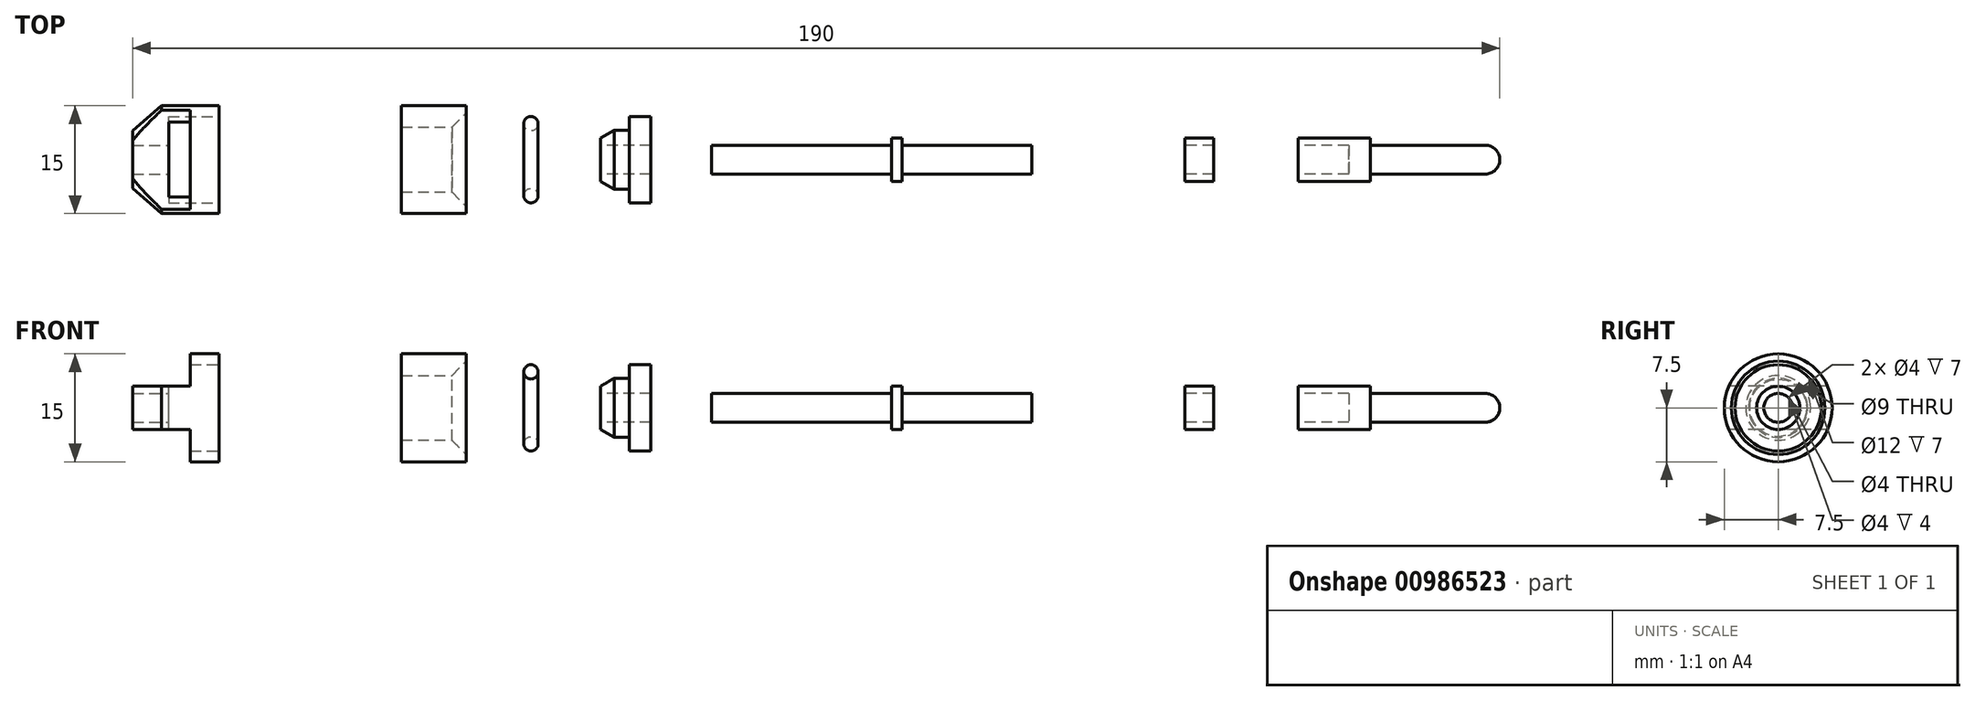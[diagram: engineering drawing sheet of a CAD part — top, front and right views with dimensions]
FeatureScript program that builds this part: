
annotation { "Feature Type Name" : "Feature", "Feature Type Description" : "" }
export const myFeature = defineFeature(function(context is Context, id is Id, definition is map)
    precondition{}
    {
        {
            var Q0;
            Q0=qCreatedBy(makeId("Front.planeOp"),FACE);
            var sketch = newSketch(context, id + "F0", { "sketchPlane" : qUnion([Q0])});
            skLineSegment(sketch, "E0", {"start": v(0, 2) * mm, "end": v(0, 6) * mm});
            skLineSegment(sketch, "E1", {"start": v(0, 6) * mm, "end": v(-3, 6) * mm});
            skLineSegment(sketch, "E2", {"start": v(-7, 3) * mm, "end": v(-7, 2) * mm});
            skLineSegment(sketch, "E3", {"start": v(-7, 2) * mm, "end": v(0, 2) * mm});
            skLineSegment(sketch, "E4", {"start": v(-20.87, 0) * mm, "end": v(7.44, 0) * mm, "construction": true});
            skLineSegment(sketch, "E5", {"start": v(-5.1, 4.1) * mm, "end": v(-3, 4.1) * mm});
            skLineSegment(sketch, "E6", {"start": v(-3, 6) * mm, "end": v(-3, 4.1) * mm});
            skLineSegment(sketch, "E7.trimOffspring", {"start": v(-5.1, 4.1) * mm, "end": v(-7, 3) * mm});
            skCircle(sketch, "E8", {"center": v(-4, 5.1) * mm, "radius": 1 * mm, "construction": true});
            skSolve(sketch);
        }
        {
            var Q0;
            Q0 = qSketchRegion(id + "F0", true);
            var Q1;
            Q1=sQuery(id+"F0.wireOp",EDGE,"E4");
            revolve(context, id + "F1", {"surfaceOperationType" : NewSurfaceOperationType.NEW, "entities" : qUnion([Q0]), "axis" : qUnion([Q1]), "revolveType" : RevolveType.FULL});
        }
        {
            var Q0;
            Q0=qCreatedBy(makeId("Front.planeOp"),FACE);
            var sketch = newSketch(context, id + "F2", { "sketchPlane" : qUnion([Q0])});
            skCircle(sketch, "E9", {"center": v(-16.65, 5) * mm, "radius": 1 * mm});
            skLineSegment(sketch, "E10", {"start": v(-20.47, 0) * mm, "end": v(-13.32, 0) * mm, "construction": true});
            skSolve(sketch);
        }
        {
            var Q0;
            Q0 = qSketchRegion(id + "F2", true);
            var Q1;
            Q1=sQuery(id+"F2.wireOp",EDGE,"E10");
            revolve(context, id + "F3", {"surfaceOperationType" : NewSurfaceOperationType.NEW, "entities" : qUnion([Q0]), "axis" : qUnion([Q1]), "revolveType" : RevolveType.FULL});
        }
        {
            var Q0;
            Q0=qCreatedBy(makeId("Front.planeOp"),FACE);
            var sketch = newSketch(context, id + "F4", { "sketchPlane" : qUnion([Q0])});
            skLineSegment(sketch, "E11", {"start": v(-21.56, 0) * mm, "end": v(-45.94, 0) * mm, "construction": true});
            skLineSegment(sketch, "E12", {"start": v(-27.65, 4.5) * mm, "end": v(-34.65, 4.5) * mm});
            skLineSegment(sketch, "E13", {"start": v(-34.65, 4.5) * mm, "end": v(-34.65, 7.5) * mm});
            skLineSegment(sketch, "E14", {"start": v(-34.65, 7.5) * mm, "end": v(-25.65, 7.5) * mm});
            skLineSegment(sketch, "E15", {"start": v(-25.65, 7.5) * mm, "end": v(-25.65, 6.5) * mm});
            skCircle(sketch, "E16", {"center": v(-25.73, 5) * mm, "radius": 1 * mm, "construction": true});
            skLineSegment(sketch, "E17", {"start": v(-27.65, 4.5) * mm, "end": v(-25.65, 6.5) * mm});
            skLineSegment(sketch, "E18", {"start": v(-27.2, 3) * mm, "end": v(-22, 6) * mm, "construction": true});
            skLineSegment(sketch, "E19", {"start": v(-22, 6) * mm, "end": v(-19.2, 6) * mm, "construction": true});
            skLineSegment(sketch, "E20", {"start": v(-19.2, 6) * mm, "end": v(-19.2, 2) * mm, "construction": true});
            skLineSegment(sketch, "E21", {"start": v(-19.2, 2) * mm, "end": v(-27.2, 2) * mm, "construction": true});
            skLineSegment(sketch, "E22", {"start": v(-27.2, 3) * mm, "end": v(-27.2, 2) * mm, "construction": true});
            skSolve(sketch);
        }
        {
            var Q0;
            Q0=makeQuery(id+"F4.imprint","IMPRINT",FACE,{"disambiguationData":[TD([[makeQuery(id+"F4.imprint","IMPRINT",EDGE,{"derivedFrom":sQuery(id+"F4.wireOp",EDGE,"E12")}),-1.0]])]});
            var Q1;
            Q1=sQuery(id+"F4.wireOp",EDGE,"E11");
            revolve(context, id + "F5", {"surfaceOperationType" : NewSurfaceOperationType.NEW, "entities" : qUnion([Q0]), "axis" : qUnion([Q1]), "revolveType" : RevolveType.FULL});
        }
        {
            var Q0;
            Q0=qCreatedBy(makeId("Front.planeOp"),FACE);
            var sketch = newSketch(context, id + "F6", { "sketchPlane" : qUnion([Q0])});
            skLineSegment(sketch, "E23", {"start": v(0.81, 0) * mm, "end": v(79.53, 0) * mm, "construction": true});
            skLineSegment(sketch, "E24.bottom", {"start": v(8.44, 0) * mm, "end": v(52.94, 0) * mm});
            skLineSegment(sketch, "E24.top", {"start": v(8.44, 2) * mm, "end": v(33.44, 2) * mm});
            skLineSegment(sketch, "E24.left", {"start": v(8.44, 0) * mm, "end": v(8.44, 2) * mm});
            skLineSegment(sketch, "E24.right", {"start": v(52.94, 0) * mm, "end": v(52.94, 2) * mm});
            skLineSegment(sketch, "E25", {"start": v(33.44, 2) * mm, "end": v(33.44, 3) * mm});
            skLineSegment(sketch, "E26", {"start": v(33.44, 3) * mm, "end": v(34.94, 3) * mm});
            skLineSegment(sketch, "E27", {"start": v(34.94, 3) * mm, "end": v(34.94, 2) * mm});
            skLineSegment(sketch, "E28.trimOffspring", {"start": v(34.94, 2) * mm, "end": v(52.94, 2) * mm});
            skSolve(sketch);
        }
        {
            var Q0;
            Q0=makeQuery(id+"F6.imprint","IMPRINT",FACE,{"disambiguationData":[TD([[makeQuery(id+"F6.imprint","IMPRINT",EDGE,{"derivedFrom":sQuery(id+"F6.wireOp",EDGE,"E24.bottom")}),1.0]])]});
            var Q1;
            Q1=sQuery(id+"F6.wireOp",EDGE,"E23");
            revolve(context, id + "F7", {"surfaceOperationType" : NewSurfaceOperationType.NEW, "entities" : qUnion([Q0]), "axis" : qUnion([Q1]), "revolveType" : RevolveType.FULL});
        }
        {
            var Q0;
            Q0=qCreatedBy(makeId("Front.planeOp"),FACE);
            var sketch = newSketch(context, id + "F8", { "sketchPlane" : qUnion([Q0])});
            skLineSegment(sketch, "E29", {"start": v(72.28, 0) * mm, "end": v(83.27, 0) * mm, "construction": true});
            skLineSegment(sketch, "E30.bottom", {"start": v(74.2, 2) * mm, "end": v(78.2, 2) * mm});
            skLineSegment(sketch, "E30.top", {"start": v(74.2, 3) * mm, "end": v(78.2, 3) * mm});
            skLineSegment(sketch, "E30.left", {"start": v(74.2, 2) * mm, "end": v(74.2, 3) * mm});
            skLineSegment(sketch, "E30.right", {"start": v(78.2, 2) * mm, "end": v(78.2, 3) * mm});
            skSolve(sketch);
        }
        {
            var Q0;
            Q0=makeQuery(id+"F8.imprint","IMPRINT",FACE,{"disambiguationData":[TD([[makeQuery(id+"F8.imprint","IMPRINT",EDGE,{"derivedFrom":sQuery(id+"F8.wireOp",EDGE,"E30.bottom")}),1.0]])]});
            var Q1;
            Q1=sQuery(id+"F8.wireOp",EDGE,"E29");
            revolve(context, id + "F9", {"surfaceOperationType" : NewSurfaceOperationType.NEW, "entities" : qUnion([Q0]), "axis" : qUnion([Q1]), "revolveType" : RevolveType.FULL});
        }
        {
            var Q0;
            Q0=qCreatedBy(makeId("Front.planeOp"),FACE);
            var sketch = newSketch(context, id + "F10", { "sketchPlane" : qUnion([Q0])});
            skLineSegment(sketch, "E31", {"start": v(90, 0) * mm, "end": v(157.92, 0) * mm, "construction": true});
            skLineSegment(sketch, "E32", {"start": v(90, 3) * mm, "end": v(100, 3) * mm});
            skLineSegment(sketch, "E33", {"start": v(118, 2) * mm, "end": v(118, 0) * mm});
            skLineSegment(sketch, "E34", {"start": v(118, 0) * mm, "end": v(97, 0) * mm});
            skLineSegment(sketch, "E35", {"start": v(97, 0) * mm, "end": v(97, 2) * mm});
            skLineSegment(sketch, "E36", {"start": v(97, 2) * mm, "end": v(90, 2) * mm});
            skLineSegment(sketch, "E37", {"start": v(90, 2) * mm, "end": v(90, 3) * mm});
            skLineSegment(sketch, "E38", {"start": v(100, 3) * mm, "end": v(100, 2) * mm});
            skLineSegment(sketch, "E39", {"start": v(100, 2) * mm, "end": v(118, 2) * mm});
            skSolve(sketch);
        }
        {
            var Q0;
            Q0=makeQuery(id+"F10.imprint","IMPRINT",FACE,{"disambiguationData":[TD([[makeQuery(id+"F10.imprint","IMPRINT",EDGE,{"derivedFrom":sQuery(id+"F10.wireOp",EDGE,"E32")}),-1.0]])]});
            var Q1;
            Q1=sQuery(id+"F10.wireOp",EDGE,"E31");
            revolve(context, id + "F11", {"surfaceOperationType" : NewSurfaceOperationType.NEW, "entities" : qUnion([Q0]), "axis" : qUnion([Q1]), "revolveType" : RevolveType.FULL});
        }
        {
            var Q0;
            Q0=qCreatedBy(makeId("Front.planeOp"),FACE);
            var sketch = newSketch(context, id + "F12", { "sketchPlane" : qUnion([Q0])});
            skLineSegment(sketch, "E40", {"start": v(0, 0) * mm, "end": v(-90.94, 0) * mm, "construction": true});
            skLineSegment(sketch, "E41", {"start": v(-60, 7.5) * mm, "end": v(-68, 7.5) * mm});
            skLineSegment(sketch, "E42", {"start": v(-72, 4) * mm, "end": v(-72, 2) * mm});
            skLineSegment(sketch, "E43", {"start": v(-72, 2) * mm, "end": v(-67, 2) * mm});
            skLineSegment(sketch, "E44", {"start": v(-67, 2) * mm, "end": v(-67, 6) * mm});
            skLineSegment(sketch, "E45", {"start": v(-67, 6) * mm, "end": v(-60, 6) * mm});
            skLineSegment(sketch, "E46", {"start": v(-60, 6) * mm, "end": v(-60, 7.5) * mm});
            skLineSegment(sketch, "E47", {"start": v(-72, 4) * mm, "end": v(-68, 7.5) * mm});
            skSolve(sketch);
        }
        {
            var Q0;
            Q0=makeQuery(id+"F12.imprint","IMPRINT",FACE,{"disambiguationData":[TD([[makeQuery(id+"F12.imprint","IMPRINT",EDGE,{"derivedFrom":sQuery(id+"F12.wireOp",EDGE,"E41")}),1.0]])]});
            var Q1;
            Q1=sQuery(id+"F12.wireOp",EDGE,"E40");
            revolve(context, id + "F13", {"surfaceOperationType" : NewSurfaceOperationType.NEW, "entities" : qUnion([Q0]), "axis" : qUnion([Q1]), "revolveType" : RevolveType.FULL});
        }
        {
            var Q0;
            Q0=qCreatedBy(makeId("Top.planeOp"),FACE);
            cPlane(context, id + "F14", {"entities" : qUnion([Q0]), "cplaneType" : CPlaneType.OFFSET, "offset" : 8 * mm, "width" : 150 * mm, "height" : 150 * mm});
        }
        {
            var Q0;
            Q0=qCreatedBy(id+"F14.planeOp",FACE);
            var sketch = newSketch(context, id + "F15", { "sketchPlane" : qUnion([Q0])});
            skLineSegment(sketch, "E48.bottom", {"start": v(-72, 7.5) * mm, "end": v(-64, 7.5) * mm});
            skLineSegment(sketch, "E48.top", {"start": v(-72, -7.5) * mm, "end": v(-64, -7.5) * mm});
            skLineSegment(sketch, "E48.left", {"start": v(-72, 7.5) * mm, "end": v(-72, -7.5) * mm});
            skLineSegment(sketch, "E48.right", {"start": v(-64, 7.5) * mm, "end": v(-64, -7.5) * mm});
            skLineSegment(sketch, "E49", {"start": v(-72, 7.5) * mm, "end": v(-60, 7.5) * mm, "construction": true});
            skLineSegment(sketch, "E50", {"start": v(-60, -7.5) * mm, "end": v(-72, -7.5) * mm, "construction": true});
            skSolve(sketch);
        }
        {
            var Q0;
            Q0=makeQuery(id+"F15.imprint","IMPRINT",FACE,{"disambiguationData":[TD([[makeQuery(id+"F15.imprint","IMPRINT",EDGE,{"derivedFrom":sQuery(id+"F15.wireOp",EDGE,"E48.bottom")}),-1.0]])]});
            extrude(context, id + "F16", {"entities" : qUnion([Q0]), "operationType" : NewBodyOperationType.REMOVE, "oppositeDirection" : true, "depth" : 5 * mm, "offsetDistance" : 25 * mm});
        }
        {
            var Q0;
            Q0=qCreatedBy(makeId("Top.planeOp"),FACE);
            cPlane(context, id + "F17", {"entities" : qUnion([Q0]), "cplaneType" : CPlaneType.OFFSET, "offset" : 8 * mm, "oppositeDirection" : true, "width" : 150 * mm, "height" : 150 * mm});
        }
        {
            var Q0;
            Q0=qCreatedBy(id+"F17.planeOp",FACE);
            var sketch = newSketch(context, id + "F18", { "sketchPlane" : qUnion([Q0])});
            skLineSegment(sketch, "E51.0", {"start": v(-72, 7.5) * mm, "end": v(-64, 7.5) * mm});
            skLineSegment(sketch, "E52.0", {"start": v(-72, 7.5) * mm, "end": v(-72, -7.5) * mm});
            skLineSegment(sketch, "E53.0", {"start": v(-64, 7.5) * mm, "end": v(-64, -7.5) * mm});
            skLineSegment(sketch, "E54.0", {"start": v(-72, -7.5) * mm, "end": v(-64, -7.5) * mm});
            skLineSegment(sketch, "E55.0.2", {"start": v(-64, -7.5) * mm, "end": v(-64, 7.5) * mm});
            skLineSegment(sketch, "E55.0.3", {"start": v(-64, 7.5) * mm, "end": v(-72, 7.5) * mm});
            skSolve(sketch);
        }
        {
            var Q0;
            Q0=makeQuery(id+"F18.imprint","IMPRINT",FACE,{"disambiguationData":[TD([[makeQuery(id+"F18.imprint","IMPRINT",EDGE,{"derivedFrom":sQuery(id+"F18.wireOp",EDGE,"E52.0")}),1.0]])]});
            extrude(context, id + "F19", {"entities" : qUnion([Q0]), "operationType" : NewBodyOperationType.REMOVE, "depth" : 5 * mm, "offsetDistance" : 25 * mm});
        }
        {
            var Q0;
            Q0=makeQuery(id+"F11.opRevolve","SWEPT_EDGE",EDGE,{"disambiguationData":[OSD([sQuery(id+"F10.wireOp",EDGE,"E33"),sQuery(id+"F10.wireOp",EDGE,"E39")])]});
            fillet(context, id + "F20", {"entities" : qUnion([Q0]), "radius" : 2 * mm, "tangentPropagation" : true, "allowEdgeOverflow" : false});
        }
    });
